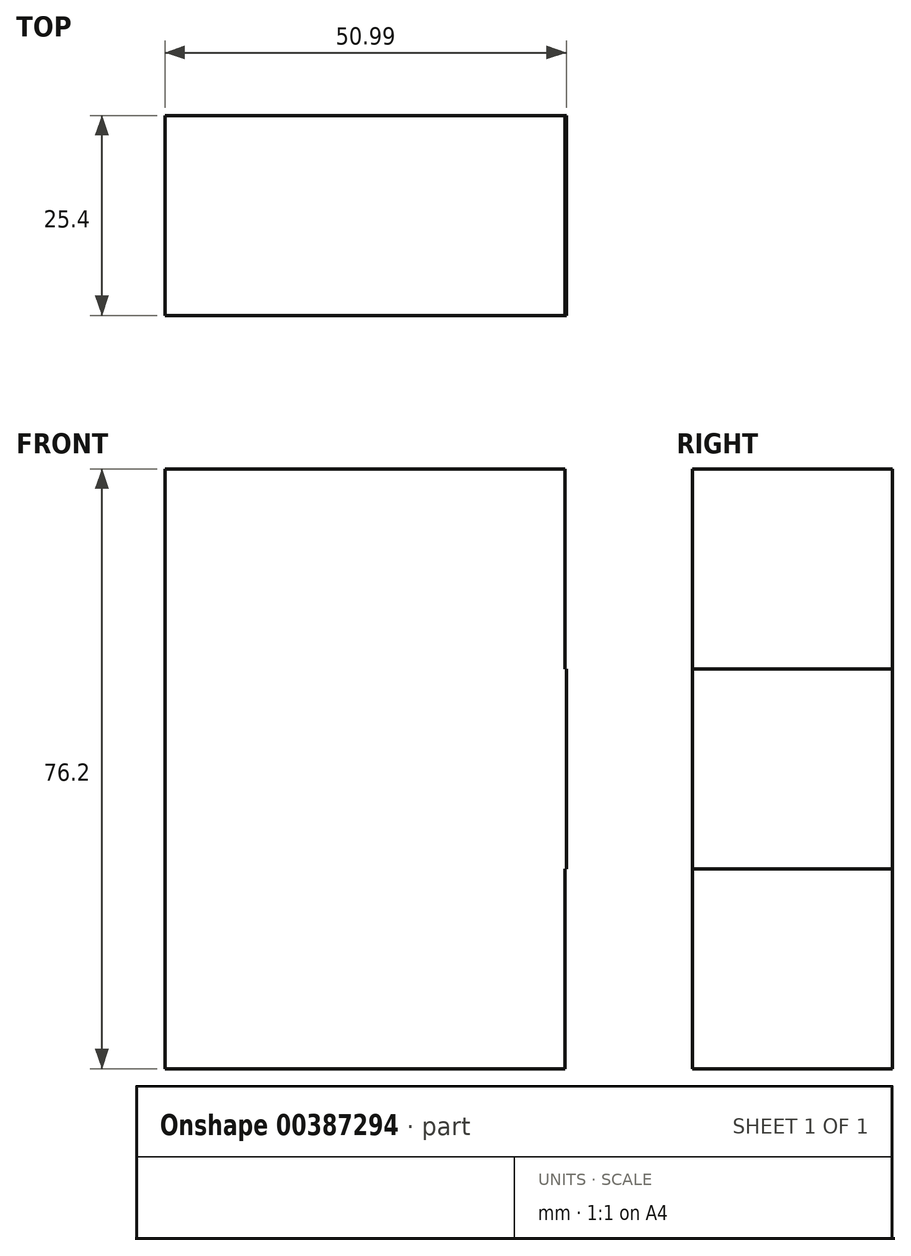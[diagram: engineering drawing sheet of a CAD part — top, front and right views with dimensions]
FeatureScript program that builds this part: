
annotation { "Feature Type Name" : "Feature", "Feature Type Description" : "" }
export const myFeature = defineFeature(function(context is Context, id is Id, definition is map)
    precondition{}
    {
        {
            var Q0;
            Q0=qCreatedBy(makeId("Front.planeOp"),FACE);
            var sketch = newSketch(context, id + "F0", { "sketchPlane" : qUnion([Q0])});
            skLineSegment(sketch, "E0.bottom", {"start": v(0, 0) * mm, "end": v(25.4, 0) * mm});
            skLineSegment(sketch, "E0.top", {"start": v(0, 25.4) * mm, "end": v(25.4, 25.4) * mm});
            skLineSegment(sketch, "E0.left", {"start": v(0, 0) * mm, "end": v(0, 25.4) * mm});
            skLineSegment(sketch, "E0.right", {"start": v(25.4, 0) * mm, "end": v(25.4, 25.4) * mm});
            skLineSegment(sketch, "E1.bottom", {"start": v(0, 0) * mm, "end": v(-25.4, 0) * mm});
            skLineSegment(sketch, "E1.top", {"start": v(0, 25.4) * mm, "end": v(-25.4, 25.4) * mm});
            skLineSegment(sketch, "E1.right", {"start": v(-25.4, 0) * mm, "end": v(-25.4, 25.4) * mm});
            skLineSegment(sketch, "E2.top", {"start": v(0, -25.4) * mm, "end": v(-25.4, -25.4) * mm});
            skLineSegment(sketch, "E2.left", {"start": v(0, 0) * mm, "end": v(0, -25.4) * mm});
            skLineSegment(sketch, "E2.right", {"start": v(-25.4, 0) * mm, "end": v(-25.4, -25.4) * mm});
            skLineSegment(sketch, "E3.bottom", {"start": v(0, 0) * mm, "end": v(25.6, 0) * mm});
            skLineSegment(sketch, "E3.top", {"start": v(0, -25.4) * mm, "end": v(25.6, -25.4) * mm});
            skLineSegment(sketch, "E3.right", {"start": v(25.6, 0) * mm, "end": v(25.6, -25.4) * mm});
            skPoint(sketch, "E4.oppositeSnap0", {"position": v(-25.4, -12.7) * mm});
            skLineSegment(sketch, "E4.top", {"start": v(0, -50.8) * mm, "end": v(-25.4, -50.8) * mm});
            skLineSegment(sketch, "E4.left", {"start": v(0, -25.4) * mm, "end": v(0, -50.8) * mm});
            skLineSegment(sketch, "E4.right", {"start": v(-25.4, -25.4) * mm, "end": v(-25.4, -50.8) * mm});
            skLineSegment(sketch, "E5.bottom", {"start": v(0, -25.4) * mm, "end": v(25.4, -25.4) * mm});
            skLineSegment(sketch, "E5.top", {"start": v(0, -50.8) * mm, "end": v(25.4, -50.8) * mm});
            skLineSegment(sketch, "E5.right", {"start": v(25.4, -25.4) * mm, "end": v(25.4, -50.8) * mm});
            skSolve(sketch);
        }
        {
            var Q0;
            Q0 = qSketchRegion(id + "F0", true);
            extrude(context, id + "F1", {"entities" : qUnion([Q0]), "depth" : 25.4 * mm});
        }
    });
